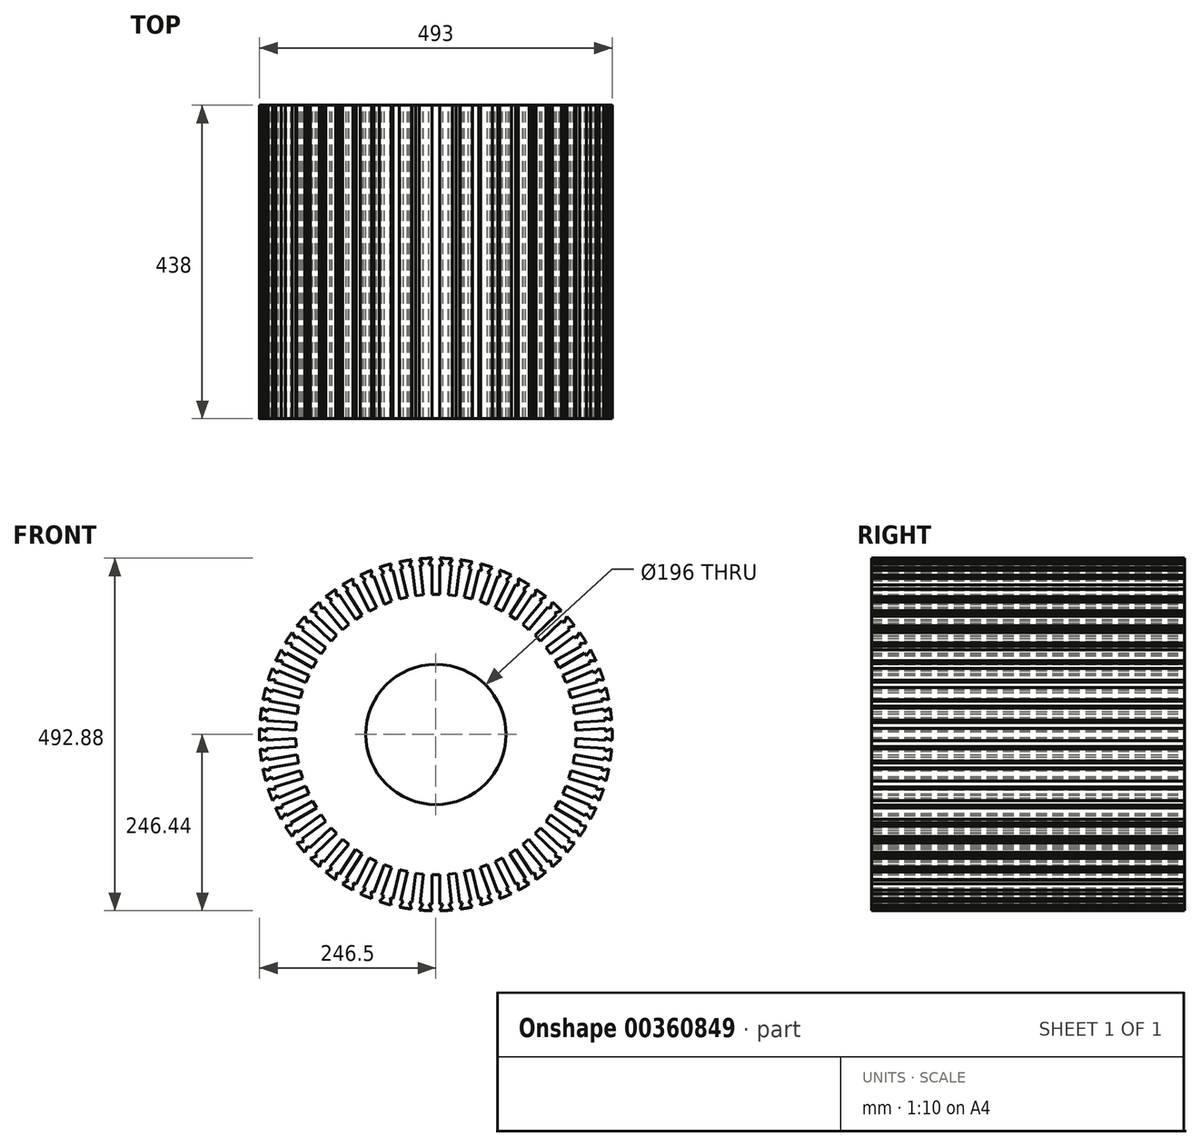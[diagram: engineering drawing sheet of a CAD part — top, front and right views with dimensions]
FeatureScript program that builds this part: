
annotation { "Feature Type Name" : "Feature", "Feature Type Description" : "" }
export const myFeature = defineFeature(function(context is Context, id is Id, definition is map)
    precondition{}
    {
        {
            var Q0;
            Q0=qCreatedBy(makeId("Front.planeOp"),FACE);
            var sketch = newSketch(context, id + "F0", { "sketchPlane" : qUnion([Q0])});
            skArc(sketch, "E0", {"start": v(-5.6, 246.44) * mm, "mid": v(-14.33, 246.08) * mm, "end": v(-23.05, 245.42) * mm});
            skLineSegment(sketch, "E1", {"start": v(0, -271.23) * mm, "end": v(0, 264.46) * mm, "construction": true});
            skLineSegment(sketch, "E2", {"start": v(0, 195.84) * mm, "end": v(-5.6, 195.84) * mm});
            skLineSegment(sketch, "E3", {"start": v(-5.6, 195.84) * mm, "end": v(-5.6, 237.27) * mm});
            skLineSegment(sketch, "E4.MirrorCS", {"start": v(5.6, 195.84) * mm, "end": v(5.6, 237.27) * mm});
            skLineSegment(sketch, "E5.MirrorCS", {"start": v(0, 195.84) * mm, "end": v(5.6, 195.84) * mm});
            skLineSegment(sketch, "E6", {"start": v(-5.6, 237.27) * mm, "end": v(-9.6, 237.27) * mm});
            skLineSegment(sketch, "E7", {"start": v(-9.6, 237.27) * mm, "end": v(-5.6, 246.44) * mm});
            skLineSegment(sketch, "E8.MirrorCS", {"start": v(9.6, 237.27) * mm, "end": v(5.6, 246.44) * mm});
            skLineSegment(sketch, "E9.MirrorCS", {"start": v(5.6, 237.27) * mm, "end": v(9.6, 237.27) * mm});
            skPoint(sketch, "E10.orphan", {"position": v(5.6, 246.44) * mm});
            skLineSegment(sketch, "E11.1.0", {"start": v(28.3, 193.86) * mm, "end": v(33.1, 235.02) * mm});
            skLineSegment(sketch, "E11.1.1", {"start": v(33.1, 235.02) * mm, "end": v(37.08, 234.55) * mm});
            skLineSegment(sketch, "E11.1.2", {"start": v(37.08, 234.55) * mm, "end": v(34.17, 244.12) * mm});
            skLineSegment(sketch, "E11.1.3", {"start": v(22.74, 194.51) * mm, "end": v(28.3, 193.86) * mm});
            skLineSegment(sketch, "E11.1.4", {"start": v(22.74, 194.51) * mm, "end": v(17.17, 195.16) * mm});
            skLineSegment(sketch, "E11.1.5", {"start": v(17.17, 195.16) * mm, "end": v(21.98, 236.32) * mm});
            skLineSegment(sketch, "E11.1.6", {"start": v(21.98, 236.32) * mm, "end": v(18.01, 236.78) * mm});
            skLineSegment(sketch, "E11.1.7", {"start": v(18.01, 236.78) * mm, "end": v(23.05, 245.42) * mm});
            skLineSegment(sketch, "E11.2.0", {"start": v(50.61, 189.27) * mm, "end": v(60.17, 229.58) * mm});
            skLineSegment(sketch, "E11.2.1", {"start": v(60.17, 229.58) * mm, "end": v(64.06, 228.66) * mm});
            skLineSegment(sketch, "E11.2.2", {"start": v(64.06, 228.66) * mm, "end": v(62.28, 238.5) * mm});
            skLineSegment(sketch, "E11.2.3", {"start": v(45.16, 190.56) * mm, "end": v(50.61, 189.27) * mm});
            skLineSegment(sketch, "E11.2.4", {"start": v(45.16, 190.56) * mm, "end": v(39.71, 191.85) * mm});
            skLineSegment(sketch, "E11.2.5", {"start": v(39.71, 191.85) * mm, "end": v(49.27, 232.17) * mm});
            skLineSegment(sketch, "E11.2.6", {"start": v(49.27, 232.17) * mm, "end": v(45.38, 233.09) * mm});
            skLineSegment(sketch, "E11.2.7", {"start": v(45.38, 233.09) * mm, "end": v(51.38, 241.09) * mm});
            skLineSegment(sketch, "E11.3.0", {"start": v(72.24, 182.11) * mm, "end": v(86.41, 221.05) * mm});
            skLineSegment(sketch, "E11.3.1", {"start": v(86.41, 221.05) * mm, "end": v(90.17, 219.68) * mm});
            skLineSegment(sketch, "E11.3.2", {"start": v(90.17, 219.68) * mm, "end": v(89.55, 229.66) * mm});
            skLineSegment(sketch, "E11.3.3", {"start": v(66.98, 184.03) * mm, "end": v(72.24, 182.11) * mm});
            skLineSegment(sketch, "E11.3.4", {"start": v(66.98, 184.03) * mm, "end": v(61.72, 185.94) * mm});
            skLineSegment(sketch, "E11.3.5", {"start": v(61.72, 185.94) * mm, "end": v(75.89, 224.88) * mm});
            skLineSegment(sketch, "E11.3.6", {"start": v(75.89, 224.88) * mm, "end": v(72.13, 226.25) * mm});
            skLineSegment(sketch, "E11.3.7", {"start": v(72.13, 226.25) * mm, "end": v(79.02, 233.49) * mm});
            skLineSegment(sketch, "E11.4.0", {"start": v(92.9, 172.5) * mm, "end": v(111.5, 209.52) * mm});
            skLineSegment(sketch, "E11.4.1", {"start": v(111.5, 209.52) * mm, "end": v(115.07, 207.72) * mm});
            skLineSegment(sketch, "E11.4.2", {"start": v(115.07, 207.72) * mm, "end": v(115.6, 217.71) * mm});
            skLineSegment(sketch, "E11.4.3", {"start": v(87.9, 175) * mm, "end": v(92.9, 172.5) * mm});
            skLineSegment(sketch, "E11.4.4", {"start": v(87.9, 175) * mm, "end": v(82.89, 177.52) * mm});
            skLineSegment(sketch, "E11.4.5", {"start": v(82.89, 177.52) * mm, "end": v(101.48, 214.55) * mm});
            skLineSegment(sketch, "E11.4.6", {"start": v(101.48, 214.55) * mm, "end": v(97.9, 216.34) * mm});
            skLineSegment(sketch, "E11.4.7", {"start": v(97.9, 216.34) * mm, "end": v(105.6, 222.74) * mm});
            skLineSegment(sketch, "E11.5.0", {"start": v(112.3, 160.54) * mm, "end": v(135.06, 195.16) * mm});
            skLineSegment(sketch, "E11.5.1", {"start": v(135.06, 195.16) * mm, "end": v(138.4, 192.96) * mm});
            skLineSegment(sketch, "E11.5.2", {"start": v(138.4, 192.96) * mm, "end": v(140.1, 202.82) * mm});
            skLineSegment(sketch, "E11.5.3", {"start": v(107.61, 163.62) * mm, "end": v(112.3, 160.54) * mm});
            skLineSegment(sketch, "E11.5.4", {"start": v(107.61, 163.62) * mm, "end": v(102.94, 166.7) * mm});
            skLineSegment(sketch, "E11.5.5", {"start": v(102.94, 166.7) * mm, "end": v(125.7, 201.31) * mm});
            skLineSegment(sketch, "E11.5.6", {"start": v(125.7, 201.31) * mm, "end": v(122.36, 203.51) * mm});
            skLineSegment(sketch, "E11.5.7", {"start": v(122.36, 203.51) * mm, "end": v(130.74, 208.97) * mm});
            skLineSegment(sketch, "E11.6.0", {"start": v(130.17, 146.42) * mm, "end": v(156.8, 178.16) * mm});
            skLineSegment(sketch, "E11.6.1", {"start": v(156.8, 178.16) * mm, "end": v(159.87, 175.59) * mm});
            skLineSegment(sketch, "E11.6.2", {"start": v(159.87, 175.59) * mm, "end": v(162.7, 185.18) * mm});
            skLineSegment(sketch, "E11.6.3", {"start": v(125.88, 150.02) * mm, "end": v(130.17, 146.42) * mm});
            skLineSegment(sketch, "E11.6.4", {"start": v(125.88, 150.02) * mm, "end": v(121.6, 153.62) * mm});
            skLineSegment(sketch, "E11.6.5", {"start": v(121.6, 153.62) * mm, "end": v(148.23, 185.36) * mm});
            skLineSegment(sketch, "E11.6.6", {"start": v(148.23, 185.36) * mm, "end": v(145.16, 187.93) * mm});
            skLineSegment(sketch, "E11.6.7", {"start": v(145.16, 187.93) * mm, "end": v(154.12, 192.38) * mm});
            skLineSegment(sketch, "E11.7.0", {"start": v(146.29, 130.32) * mm, "end": v(176.43, 158.75) * mm});
            skLineSegment(sketch, "E11.7.1", {"start": v(176.43, 158.75) * mm, "end": v(179.17, 155.84) * mm});
            skLineSegment(sketch, "E11.7.2", {"start": v(179.17, 155.84) * mm, "end": v(183.1, 165.04) * mm});
            skLineSegment(sketch, "E11.7.3", {"start": v(142.45, 134.4) * mm, "end": v(146.29, 130.32) * mm});
            skLineSegment(sketch, "E11.7.4", {"start": v(142.45, 134.4) * mm, "end": v(138.6, 138.46) * mm});
            skLineSegment(sketch, "E11.7.5", {"start": v(138.6, 138.46) * mm, "end": v(168.74, 166.9) * mm});
            skLineSegment(sketch, "E11.7.6", {"start": v(168.74, 166.9) * mm, "end": v(166, 169.8) * mm});
            skLineSegment(sketch, "E11.7.7", {"start": v(166, 169.8) * mm, "end": v(175.4, 173.19) * mm});
            skLineSegment(sketch, "E11.8.0", {"start": v(160.43, 112.45) * mm, "end": v(193.66, 137.2) * mm});
            skLineSegment(sketch, "E11.8.1", {"start": v(193.66, 137.2) * mm, "end": v(196.05, 133.99) * mm});
            skLineSegment(sketch, "E11.8.2", {"start": v(196.05, 133.99) * mm, "end": v(201.02, 142.67) * mm});
            skLineSegment(sketch, "E11.8.3", {"start": v(157.08, 116.95) * mm, "end": v(160.43, 112.45) * mm});
            skLineSegment(sketch, "E11.8.4", {"start": v(157.08, 116.95) * mm, "end": v(153.74, 121.44) * mm});
            skLineSegment(sketch, "E11.8.5", {"start": v(153.74, 121.44) * mm, "end": v(186.98, 146.18) * mm});
            skLineSegment(sketch, "E11.8.6", {"start": v(186.98, 146.18) * mm, "end": v(184.59, 149.39) * mm});
            skLineSegment(sketch, "E11.8.7", {"start": v(184.59, 149.39) * mm, "end": v(194.33, 151.65) * mm});
            skLineSegment(sketch, "E11.9.0", {"start": v(172.4, 93.07) * mm, "end": v(208.28, 113.79) * mm});
            skLineSegment(sketch, "E11.9.1", {"start": v(208.28, 113.79) * mm, "end": v(210.28, 110.32) * mm});
            skLineSegment(sketch, "E11.9.2", {"start": v(210.28, 110.32) * mm, "end": v(216.22, 118.37) * mm});
            skLineSegment(sketch, "E11.9.3", {"start": v(169.6, 97.92) * mm, "end": v(172.4, 93.07) * mm});
            skLineSegment(sketch, "E11.9.4", {"start": v(169.6, 97.92) * mm, "end": v(166.8, 102.77) * mm});
            skLineSegment(sketch, "E11.9.5", {"start": v(166.8, 102.77) * mm, "end": v(202.68, 123.49) * mm});
            skLineSegment(sketch, "E11.9.6", {"start": v(202.68, 123.49) * mm, "end": v(200.68, 126.95) * mm});
            skLineSegment(sketch, "E11.9.7", {"start": v(200.68, 126.95) * mm, "end": v(210.62, 128.07) * mm});
            skLineSegment(sketch, "E11.10.0", {"start": v(182.04, 72.42) * mm, "end": v(220.08, 88.84) * mm});
            skLineSegment(sketch, "E11.10.1", {"start": v(220.08, 88.84) * mm, "end": v(221.67, 85.16) * mm});
            skLineSegment(sketch, "E11.10.2", {"start": v(221.67, 85.16) * mm, "end": v(228.5, 92.47) * mm});
            skLineSegment(sketch, "E11.10.3", {"start": v(179.82, 77.57) * mm, "end": v(182.04, 72.42) * mm});
            skLineSegment(sketch, "E11.10.4", {"start": v(179.82, 77.57) * mm, "end": v(177.6, 82.7) * mm});
            skLineSegment(sketch, "E11.10.5", {"start": v(177.6, 82.7) * mm, "end": v(215.65, 99.12) * mm});
            skLineSegment(sketch, "E11.10.6", {"start": v(215.65, 99.12) * mm, "end": v(214.06, 102.8) * mm});
            skLineSegment(sketch, "E11.10.7", {"start": v(214.06, 102.8) * mm, "end": v(224.06, 102.75) * mm});
            skLineSegment(sketch, "E11.11.0", {"start": v(189.22, 50.8) * mm, "end": v(228.9, 62.69) * mm});
            skLineSegment(sketch, "E11.11.1", {"start": v(228.9, 62.69) * mm, "end": v(230.06, 58.85) * mm});
            skLineSegment(sketch, "E11.11.2", {"start": v(230.06, 58.85) * mm, "end": v(237.69, 65.31) * mm});
            skLineSegment(sketch, "E11.11.3", {"start": v(187.6, 56.17) * mm, "end": v(189.22, 50.8) * mm});
            skLineSegment(sketch, "E11.11.4", {"start": v(187.6, 56.17) * mm, "end": v(186, 61.53) * mm});
            skLineSegment(sketch, "E11.11.5", {"start": v(186, 61.53) * mm, "end": v(225.7, 73.41) * mm});
            skLineSegment(sketch, "E11.11.6", {"start": v(225.7, 73.41) * mm, "end": v(224.55, 77.25) * mm});
            skLineSegment(sketch, "E11.11.7", {"start": v(224.55, 77.25) * mm, "end": v(234.48, 76.04) * mm});
            skLineSegment(sketch, "E11.12.0", {"start": v(193.83, 28.5) * mm, "end": v(234.64, 35.69) * mm});
            skLineSegment(sketch, "E11.12.1", {"start": v(234.64, 35.69) * mm, "end": v(235.33, 31.75) * mm});
            skLineSegment(sketch, "E11.12.2", {"start": v(235.33, 31.75) * mm, "end": v(243.66, 37.28) * mm});
            skLineSegment(sketch, "E11.12.3", {"start": v(192.86, 34) * mm, "end": v(193.83, 28.5) * mm});
            skLineSegment(sketch, "E11.12.4", {"start": v(192.86, 34) * mm, "end": v(191.89, 39.52) * mm});
            skLineSegment(sketch, "E11.12.5", {"start": v(191.89, 39.52) * mm, "end": v(232.7, 46.72) * mm});
            skLineSegment(sketch, "E11.12.6", {"start": v(232.7, 46.72) * mm, "end": v(232, 50.66) * mm});
            skLineSegment(sketch, "E11.12.7", {"start": v(232, 50.66) * mm, "end": v(241.72, 48.3) * mm});
            skLineSegment(sketch, "E11.13.0", {"start": v(195.83, 5.8) * mm, "end": v(237.2, 8.2) * mm});
            skLineSegment(sketch, "E11.13.1", {"start": v(237.2, 8.2) * mm, "end": v(237.43, 4.21) * mm});
            skLineSegment(sketch, "E11.13.2", {"start": v(237.43, 4.21) * mm, "end": v(246.35, 8.74) * mm});
            skLineSegment(sketch, "E11.13.3", {"start": v(195.5, 11.39) * mm, "end": v(195.83, 5.8) * mm});
            skLineSegment(sketch, "E11.13.4", {"start": v(195.5, 11.39) * mm, "end": v(195.18, 16.98) * mm});
            skLineSegment(sketch, "E11.13.5", {"start": v(195.18, 16.98) * mm, "end": v(236.54, 19.39) * mm});
            skLineSegment(sketch, "E11.13.6", {"start": v(236.54, 19.39) * mm, "end": v(236.31, 23.38) * mm});
            skLineSegment(sketch, "E11.13.7", {"start": v(236.31, 23.38) * mm, "end": v(245.7, 19.92) * mm});
            skLineSegment(sketch, "E11.14.0", {"start": v(195.18, -16.98) * mm, "end": v(236.54, -19.39) * mm});
            skLineSegment(sketch, "E11.14.1", {"start": v(236.54, -19.39) * mm, "end": v(236.31, -23.38) * mm});
            skLineSegment(sketch, "E11.14.2", {"start": v(236.31, -23.38) * mm, "end": v(245.7, -19.92) * mm});
            skLineSegment(sketch, "E11.14.3", {"start": v(195.5, -11.39) * mm, "end": v(195.18, -16.98) * mm});
            skLineSegment(sketch, "E11.14.4", {"start": v(195.5, -11.39) * mm, "end": v(195.83, -5.8) * mm});
            skLineSegment(sketch, "E11.14.5", {"start": v(195.83, -5.8) * mm, "end": v(237.2, -8.2) * mm});
            skLineSegment(sketch, "E11.14.6", {"start": v(237.2, -8.2) * mm, "end": v(237.43, -4.21) * mm});
            skLineSegment(sketch, "E11.14.7", {"start": v(237.43, -4.21) * mm, "end": v(246.35, -8.74) * mm});
            skLineSegment(sketch, "E11.15.0", {"start": v(191.89, -39.52) * mm, "end": v(232.7, -46.72) * mm});
            skLineSegment(sketch, "E11.15.1", {"start": v(232.7, -46.72) * mm, "end": v(232, -50.66) * mm});
            skLineSegment(sketch, "E11.15.2", {"start": v(232, -50.66) * mm, "end": v(241.72, -48.3) * mm});
            skLineSegment(sketch, "E11.15.3", {"start": v(192.86, -34) * mm, "end": v(191.89, -39.52) * mm});
            skLineSegment(sketch, "E11.15.4", {"start": v(192.86, -34) * mm, "end": v(193.83, -28.5) * mm});
            skLineSegment(sketch, "E11.15.5", {"start": v(193.83, -28.5) * mm, "end": v(234.64, -35.69) * mm});
            skLineSegment(sketch, "E11.15.6", {"start": v(234.64, -35.69) * mm, "end": v(235.33, -31.75) * mm});
            skLineSegment(sketch, "E11.15.7", {"start": v(235.33, -31.75) * mm, "end": v(243.66, -37.28) * mm});
            skLineSegment(sketch, "E11.16.0", {"start": v(186, -61.53) * mm, "end": v(225.7, -73.41) * mm});
            skLineSegment(sketch, "E11.16.1", {"start": v(225.7, -73.41) * mm, "end": v(224.55, -77.25) * mm});
            skLineSegment(sketch, "E11.16.2", {"start": v(224.55, -77.25) * mm, "end": v(234.48, -76.04) * mm});
            skLineSegment(sketch, "E11.16.3", {"start": v(187.6, -56.17) * mm, "end": v(186, -61.53) * mm});
            skLineSegment(sketch, "E11.16.4", {"start": v(187.6, -56.17) * mm, "end": v(189.22, -50.8) * mm});
            skLineSegment(sketch, "E11.16.5", {"start": v(189.22, -50.8) * mm, "end": v(228.9, -62.69) * mm});
            skLineSegment(sketch, "E11.16.6", {"start": v(228.9, -62.69) * mm, "end": v(230.06, -58.85) * mm});
            skLineSegment(sketch, "E11.16.7", {"start": v(230.06, -58.85) * mm, "end": v(237.69, -65.31) * mm});
            skLineSegment(sketch, "E11.17.0", {"start": v(177.6, -82.7) * mm, "end": v(215.65, -99.12) * mm});
            skLineSegment(sketch, "E11.17.1", {"start": v(215.65, -99.12) * mm, "end": v(214.06, -102.8) * mm});
            skLineSegment(sketch, "E11.17.2", {"start": v(214.06, -102.8) * mm, "end": v(224.06, -102.75) * mm});
            skLineSegment(sketch, "E11.17.3", {"start": v(179.82, -77.57) * mm, "end": v(177.6, -82.7) * mm});
            skLineSegment(sketch, "E11.17.4", {"start": v(179.82, -77.57) * mm, "end": v(182.04, -72.42) * mm});
            skLineSegment(sketch, "E11.17.5", {"start": v(182.04, -72.42) * mm, "end": v(220.08, -88.84) * mm});
            skLineSegment(sketch, "E11.17.6", {"start": v(220.08, -88.84) * mm, "end": v(221.67, -85.16) * mm});
            skLineSegment(sketch, "E11.17.7", {"start": v(221.67, -85.16) * mm, "end": v(228.5, -92.47) * mm});
            skLineSegment(sketch, "E11.18.0", {"start": v(166.8, -102.77) * mm, "end": v(202.68, -123.49) * mm});
            skLineSegment(sketch, "E11.18.1", {"start": v(202.68, -123.49) * mm, "end": v(200.68, -126.95) * mm});
            skLineSegment(sketch, "E11.18.2", {"start": v(200.68, -126.95) * mm, "end": v(210.62, -128.07) * mm});
            skLineSegment(sketch, "E11.18.3", {"start": v(169.6, -97.92) * mm, "end": v(166.8, -102.77) * mm});
            skLineSegment(sketch, "E11.18.4", {"start": v(169.6, -97.92) * mm, "end": v(172.4, -93.07) * mm});
            skLineSegment(sketch, "E11.18.5", {"start": v(172.4, -93.07) * mm, "end": v(208.28, -113.79) * mm});
            skLineSegment(sketch, "E11.18.6", {"start": v(208.28, -113.79) * mm, "end": v(210.28, -110.32) * mm});
            skLineSegment(sketch, "E11.18.7", {"start": v(210.28, -110.32) * mm, "end": v(216.22, -118.37) * mm});
            skLineSegment(sketch, "E11.19.0", {"start": v(153.74, -121.44) * mm, "end": v(186.98, -146.18) * mm});
            skLineSegment(sketch, "E11.19.1", {"start": v(186.98, -146.18) * mm, "end": v(184.59, -149.39) * mm});
            skLineSegment(sketch, "E11.19.2", {"start": v(184.59, -149.39) * mm, "end": v(194.33, -151.65) * mm});
            skLineSegment(sketch, "E11.19.3", {"start": v(157.08, -116.95) * mm, "end": v(153.74, -121.44) * mm});
            skLineSegment(sketch, "E11.19.4", {"start": v(157.08, -116.95) * mm, "end": v(160.43, -112.45) * mm});
            skLineSegment(sketch, "E11.19.5", {"start": v(160.43, -112.45) * mm, "end": v(193.66, -137.2) * mm});
            skLineSegment(sketch, "E11.19.6", {"start": v(193.66, -137.2) * mm, "end": v(196.05, -133.99) * mm});
            skLineSegment(sketch, "E11.19.7", {"start": v(196.05, -133.99) * mm, "end": v(201.02, -142.67) * mm});
            skLineSegment(sketch, "E11.20.0", {"start": v(138.6, -138.46) * mm, "end": v(168.74, -166.9) * mm});
            skLineSegment(sketch, "E11.20.1", {"start": v(168.74, -166.9) * mm, "end": v(166, -169.8) * mm});
            skLineSegment(sketch, "E11.20.2", {"start": v(166, -169.8) * mm, "end": v(175.4, -173.19) * mm});
            skLineSegment(sketch, "E11.20.3", {"start": v(142.45, -134.4) * mm, "end": v(138.6, -138.46) * mm});
            skLineSegment(sketch, "E11.20.4", {"start": v(142.45, -134.4) * mm, "end": v(146.29, -130.32) * mm});
            skLineSegment(sketch, "E11.20.5", {"start": v(146.29, -130.32) * mm, "end": v(176.43, -158.75) * mm});
            skLineSegment(sketch, "E11.20.6", {"start": v(176.43, -158.75) * mm, "end": v(179.17, -155.84) * mm});
            skLineSegment(sketch, "E11.20.7", {"start": v(179.17, -155.84) * mm, "end": v(183.1, -165.04) * mm});
            skLineSegment(sketch, "E11.21.0", {"start": v(121.6, -153.62) * mm, "end": v(148.23, -185.36) * mm});
            skLineSegment(sketch, "E11.21.1", {"start": v(148.23, -185.36) * mm, "end": v(145.16, -187.93) * mm});
            skLineSegment(sketch, "E11.21.2", {"start": v(145.16, -187.93) * mm, "end": v(154.12, -192.38) * mm});
            skLineSegment(sketch, "E11.21.3", {"start": v(125.88, -150.02) * mm, "end": v(121.6, -153.62) * mm});
            skLineSegment(sketch, "E11.21.4", {"start": v(125.88, -150.02) * mm, "end": v(130.17, -146.42) * mm});
            skLineSegment(sketch, "E11.21.5", {"start": v(130.17, -146.42) * mm, "end": v(156.8, -178.16) * mm});
            skLineSegment(sketch, "E11.21.6", {"start": v(156.8, -178.16) * mm, "end": v(159.87, -175.59) * mm});
            skLineSegment(sketch, "E11.21.7", {"start": v(159.87, -175.59) * mm, "end": v(162.7, -185.18) * mm});
            skLineSegment(sketch, "E11.22.0", {"start": v(102.94, -166.7) * mm, "end": v(125.7, -201.31) * mm});
            skLineSegment(sketch, "E11.22.1", {"start": v(125.7, -201.31) * mm, "end": v(122.36, -203.51) * mm});
            skLineSegment(sketch, "E11.22.2", {"start": v(122.36, -203.51) * mm, "end": v(130.74, -208.97) * mm});
            skLineSegment(sketch, "E11.22.3", {"start": v(107.61, -163.62) * mm, "end": v(102.94, -166.7) * mm});
            skLineSegment(sketch, "E11.22.4", {"start": v(107.61, -163.62) * mm, "end": v(112.3, -160.54) * mm});
            skLineSegment(sketch, "E11.22.5", {"start": v(112.3, -160.54) * mm, "end": v(135.06, -195.16) * mm});
            skLineSegment(sketch, "E11.22.6", {"start": v(135.06, -195.16) * mm, "end": v(138.4, -192.96) * mm});
            skLineSegment(sketch, "E11.22.7", {"start": v(138.4, -192.96) * mm, "end": v(140.1, -202.82) * mm});
            skLineSegment(sketch, "E11.23.0", {"start": v(82.89, -177.52) * mm, "end": v(101.48, -214.55) * mm});
            skLineSegment(sketch, "E11.23.1", {"start": v(101.48, -214.55) * mm, "end": v(97.9, -216.34) * mm});
            skLineSegment(sketch, "E11.23.2", {"start": v(97.9, -216.34) * mm, "end": v(105.6, -222.74) * mm});
            skLineSegment(sketch, "E11.23.3", {"start": v(87.9, -175) * mm, "end": v(82.89, -177.52) * mm});
            skLineSegment(sketch, "E11.23.4", {"start": v(87.9, -175) * mm, "end": v(92.9, -172.5) * mm});
            skLineSegment(sketch, "E11.23.5", {"start": v(92.9, -172.5) * mm, "end": v(111.5, -209.52) * mm});
            skLineSegment(sketch, "E11.23.6", {"start": v(111.5, -209.52) * mm, "end": v(115.07, -207.72) * mm});
            skLineSegment(sketch, "E11.23.7", {"start": v(115.07, -207.72) * mm, "end": v(115.6, -217.71) * mm});
            skLineSegment(sketch, "E11.24.0", {"start": v(61.72, -185.94) * mm, "end": v(75.89, -224.88) * mm});
            skLineSegment(sketch, "E11.24.1", {"start": v(75.89, -224.88) * mm, "end": v(72.13, -226.25) * mm});
            skLineSegment(sketch, "E11.24.2", {"start": v(72.13, -226.25) * mm, "end": v(79.02, -233.49) * mm});
            skLineSegment(sketch, "E11.24.3", {"start": v(66.98, -184.03) * mm, "end": v(61.72, -185.94) * mm});
            skLineSegment(sketch, "E11.24.4", {"start": v(66.98, -184.03) * mm, "end": v(72.24, -182.11) * mm});
            skLineSegment(sketch, "E11.24.5", {"start": v(72.24, -182.11) * mm, "end": v(86.41, -221.05) * mm});
            skLineSegment(sketch, "E11.24.6", {"start": v(86.41, -221.05) * mm, "end": v(90.17, -219.68) * mm});
            skLineSegment(sketch, "E11.24.7", {"start": v(90.17, -219.68) * mm, "end": v(89.55, -229.66) * mm});
            skLineSegment(sketch, "E11.25.0", {"start": v(39.71, -191.85) * mm, "end": v(49.27, -232.17) * mm});
            skLineSegment(sketch, "E11.25.1", {"start": v(49.27, -232.17) * mm, "end": v(45.38, -233.09) * mm});
            skLineSegment(sketch, "E11.25.2", {"start": v(45.38, -233.09) * mm, "end": v(51.38, -241.09) * mm});
            skLineSegment(sketch, "E11.25.3", {"start": v(45.16, -190.56) * mm, "end": v(39.71, -191.85) * mm});
            skLineSegment(sketch, "E11.25.4", {"start": v(45.16, -190.56) * mm, "end": v(50.61, -189.27) * mm});
            skLineSegment(sketch, "E11.25.5", {"start": v(50.61, -189.27) * mm, "end": v(60.17, -229.58) * mm});
            skLineSegment(sketch, "E11.25.6", {"start": v(60.17, -229.58) * mm, "end": v(64.06, -228.66) * mm});
            skLineSegment(sketch, "E11.25.7", {"start": v(64.06, -228.66) * mm, "end": v(62.28, -238.5) * mm});
            skLineSegment(sketch, "E11.26.0", {"start": v(17.17, -195.16) * mm, "end": v(21.98, -236.32) * mm});
            skLineSegment(sketch, "E11.26.1", {"start": v(21.98, -236.32) * mm, "end": v(18.01, -236.78) * mm});
            skLineSegment(sketch, "E11.26.2", {"start": v(18.01, -236.78) * mm, "end": v(23.05, -245.42) * mm});
            skLineSegment(sketch, "E11.26.3", {"start": v(22.74, -194.51) * mm, "end": v(17.17, -195.16) * mm});
            skLineSegment(sketch, "E11.26.4", {"start": v(22.74, -194.51) * mm, "end": v(28.3, -193.86) * mm});
            skLineSegment(sketch, "E11.26.5", {"start": v(28.3, -193.86) * mm, "end": v(33.1, -235.02) * mm});
            skLineSegment(sketch, "E11.26.6", {"start": v(33.1, -235.02) * mm, "end": v(37.08, -234.55) * mm});
            skLineSegment(sketch, "E11.26.7", {"start": v(37.08, -234.55) * mm, "end": v(34.17, -244.12) * mm});
            skLineSegment(sketch, "E11.27.0", {"start": v(-5.6, -195.84) * mm, "end": v(-5.6, -237.27) * mm});
            skLineSegment(sketch, "E11.27.1", {"start": v(-5.6, -237.27) * mm, "end": v(-9.6, -237.27) * mm});
            skLineSegment(sketch, "E11.27.2", {"start": v(-9.6, -237.27) * mm, "end": v(-5.6, -246.44) * mm});
            skLineSegment(sketch, "E11.27.3", {"start": v(0, -195.84) * mm, "end": v(-5.6, -195.84) * mm});
            skLineSegment(sketch, "E11.27.4", {"start": v(0, -195.84) * mm, "end": v(5.6, -195.84) * mm});
            skLineSegment(sketch, "E11.27.5", {"start": v(5.6, -195.84) * mm, "end": v(5.6, -237.27) * mm});
            skLineSegment(sketch, "E11.27.6", {"start": v(5.6, -237.27) * mm, "end": v(9.6, -237.27) * mm});
            skLineSegment(sketch, "E11.27.7", {"start": v(9.6, -237.27) * mm, "end": v(5.6, -246.44) * mm});
            skLineSegment(sketch, "E11.28.0", {"start": v(-28.3, -193.86) * mm, "end": v(-33.1, -235.02) * mm});
            skLineSegment(sketch, "E11.28.1", {"start": v(-33.1, -235.02) * mm, "end": v(-37.08, -234.55) * mm});
            skLineSegment(sketch, "E11.28.2", {"start": v(-37.08, -234.55) * mm, "end": v(-34.17, -244.12) * mm});
            skLineSegment(sketch, "E11.28.3", {"start": v(-22.74, -194.51) * mm, "end": v(-28.3, -193.86) * mm});
            skLineSegment(sketch, "E11.28.4", {"start": v(-22.74, -194.51) * mm, "end": v(-17.17, -195.16) * mm});
            skLineSegment(sketch, "E11.28.5", {"start": v(-17.17, -195.16) * mm, "end": v(-21.98, -236.32) * mm});
            skLineSegment(sketch, "E11.28.6", {"start": v(-21.98, -236.32) * mm, "end": v(-18.01, -236.78) * mm});
            skLineSegment(sketch, "E11.28.7", {"start": v(-18.01, -236.78) * mm, "end": v(-23.05, -245.42) * mm});
            skLineSegment(sketch, "E11.29.0", {"start": v(-50.61, -189.27) * mm, "end": v(-60.17, -229.58) * mm});
            skLineSegment(sketch, "E11.29.1", {"start": v(-60.17, -229.58) * mm, "end": v(-64.06, -228.66) * mm});
            skLineSegment(sketch, "E11.29.2", {"start": v(-64.06, -228.66) * mm, "end": v(-62.28, -238.5) * mm});
            skLineSegment(sketch, "E11.29.3", {"start": v(-45.16, -190.56) * mm, "end": v(-50.61, -189.27) * mm});
            skLineSegment(sketch, "E11.29.4", {"start": v(-45.16, -190.56) * mm, "end": v(-39.71, -191.85) * mm});
            skLineSegment(sketch, "E11.29.5", {"start": v(-39.71, -191.85) * mm, "end": v(-49.27, -232.17) * mm});
            skLineSegment(sketch, "E11.29.6", {"start": v(-49.27, -232.17) * mm, "end": v(-45.38, -233.09) * mm});
            skLineSegment(sketch, "E11.29.7", {"start": v(-45.38, -233.09) * mm, "end": v(-51.38, -241.09) * mm});
            skLineSegment(sketch, "E11.30.0", {"start": v(-72.24, -182.11) * mm, "end": v(-86.41, -221.05) * mm});
            skLineSegment(sketch, "E11.30.1", {"start": v(-86.41, -221.05) * mm, "end": v(-90.17, -219.68) * mm});
            skLineSegment(sketch, "E11.30.2", {"start": v(-90.17, -219.68) * mm, "end": v(-89.55, -229.66) * mm});
            skLineSegment(sketch, "E11.30.3", {"start": v(-66.98, -184.03) * mm, "end": v(-72.24, -182.11) * mm});
            skLineSegment(sketch, "E11.30.4", {"start": v(-66.98, -184.03) * mm, "end": v(-61.72, -185.94) * mm});
            skLineSegment(sketch, "E11.30.5", {"start": v(-61.72, -185.94) * mm, "end": v(-75.89, -224.88) * mm});
            skLineSegment(sketch, "E11.30.6", {"start": v(-75.89, -224.88) * mm, "end": v(-72.13, -226.25) * mm});
            skLineSegment(sketch, "E11.30.7", {"start": v(-72.13, -226.25) * mm, "end": v(-79.02, -233.49) * mm});
            skLineSegment(sketch, "E11.31.0", {"start": v(-92.9, -172.5) * mm, "end": v(-111.5, -209.52) * mm});
            skLineSegment(sketch, "E11.31.1", {"start": v(-111.5, -209.52) * mm, "end": v(-115.07, -207.72) * mm});
            skLineSegment(sketch, "E11.31.2", {"start": v(-115.07, -207.72) * mm, "end": v(-115.6, -217.71) * mm});
            skLineSegment(sketch, "E11.31.3", {"start": v(-87.9, -175) * mm, "end": v(-92.9, -172.5) * mm});
            skLineSegment(sketch, "E11.31.4", {"start": v(-87.9, -175) * mm, "end": v(-82.89, -177.52) * mm});
            skLineSegment(sketch, "E11.31.5", {"start": v(-82.89, -177.52) * mm, "end": v(-101.48, -214.55) * mm});
            skLineSegment(sketch, "E11.31.6", {"start": v(-101.48, -214.55) * mm, "end": v(-97.9, -216.34) * mm});
            skLineSegment(sketch, "E11.31.7", {"start": v(-97.9, -216.34) * mm, "end": v(-105.6, -222.74) * mm});
            skLineSegment(sketch, "E11.32.0", {"start": v(-112.3, -160.54) * mm, "end": v(-135.06, -195.16) * mm});
            skLineSegment(sketch, "E11.32.1", {"start": v(-135.06, -195.16) * mm, "end": v(-138.4, -192.96) * mm});
            skLineSegment(sketch, "E11.32.2", {"start": v(-138.4, -192.96) * mm, "end": v(-140.1, -202.82) * mm});
            skLineSegment(sketch, "E11.32.3", {"start": v(-107.61, -163.62) * mm, "end": v(-112.3, -160.54) * mm});
            skLineSegment(sketch, "E11.32.4", {"start": v(-107.61, -163.62) * mm, "end": v(-102.94, -166.7) * mm});
            skLineSegment(sketch, "E11.32.5", {"start": v(-102.94, -166.7) * mm, "end": v(-125.7, -201.31) * mm});
            skLineSegment(sketch, "E11.32.6", {"start": v(-125.7, -201.31) * mm, "end": v(-122.36, -203.51) * mm});
            skLineSegment(sketch, "E11.32.7", {"start": v(-122.36, -203.51) * mm, "end": v(-130.74, -208.97) * mm});
            skLineSegment(sketch, "E11.33.0", {"start": v(-130.17, -146.42) * mm, "end": v(-156.8, -178.16) * mm});
            skLineSegment(sketch, "E11.33.1", {"start": v(-156.8, -178.16) * mm, "end": v(-159.87, -175.59) * mm});
            skLineSegment(sketch, "E11.33.2", {"start": v(-159.87, -175.59) * mm, "end": v(-162.7, -185.18) * mm});
            skLineSegment(sketch, "E11.33.3", {"start": v(-125.88, -150.02) * mm, "end": v(-130.17, -146.42) * mm});
            skLineSegment(sketch, "E11.33.4", {"start": v(-125.88, -150.02) * mm, "end": v(-121.6, -153.62) * mm});
            skLineSegment(sketch, "E11.33.5", {"start": v(-121.6, -153.62) * mm, "end": v(-148.23, -185.36) * mm});
            skLineSegment(sketch, "E11.33.6", {"start": v(-148.23, -185.36) * mm, "end": v(-145.16, -187.93) * mm});
            skLineSegment(sketch, "E11.33.7", {"start": v(-145.16, -187.93) * mm, "end": v(-154.12, -192.38) * mm});
            skLineSegment(sketch, "E11.34.0", {"start": v(-146.29, -130.32) * mm, "end": v(-176.43, -158.75) * mm});
            skLineSegment(sketch, "E11.34.1", {"start": v(-176.43, -158.75) * mm, "end": v(-179.17, -155.84) * mm});
            skLineSegment(sketch, "E11.34.2", {"start": v(-179.17, -155.84) * mm, "end": v(-183.1, -165.04) * mm});
            skLineSegment(sketch, "E11.34.3", {"start": v(-142.45, -134.4) * mm, "end": v(-146.29, -130.32) * mm});
            skLineSegment(sketch, "E11.34.4", {"start": v(-142.45, -134.4) * mm, "end": v(-138.6, -138.46) * mm});
            skLineSegment(sketch, "E11.34.5", {"start": v(-138.6, -138.46) * mm, "end": v(-168.74, -166.9) * mm});
            skLineSegment(sketch, "E11.34.6", {"start": v(-168.74, -166.9) * mm, "end": v(-166, -169.8) * mm});
            skLineSegment(sketch, "E11.34.7", {"start": v(-166, -169.8) * mm, "end": v(-175.4, -173.19) * mm});
            skLineSegment(sketch, "E11.35.0", {"start": v(-160.43, -112.45) * mm, "end": v(-193.66, -137.2) * mm});
            skLineSegment(sketch, "E11.35.1", {"start": v(-193.66, -137.2) * mm, "end": v(-196.05, -133.99) * mm});
            skLineSegment(sketch, "E11.35.2", {"start": v(-196.05, -133.99) * mm, "end": v(-201.02, -142.67) * mm});
            skLineSegment(sketch, "E11.35.3", {"start": v(-157.08, -116.95) * mm, "end": v(-160.43, -112.45) * mm});
            skLineSegment(sketch, "E11.35.4", {"start": v(-157.08, -116.95) * mm, "end": v(-153.74, -121.44) * mm});
            skLineSegment(sketch, "E11.35.5", {"start": v(-153.74, -121.44) * mm, "end": v(-186.98, -146.18) * mm});
            skLineSegment(sketch, "E11.35.6", {"start": v(-186.98, -146.18) * mm, "end": v(-184.59, -149.39) * mm});
            skLineSegment(sketch, "E11.35.7", {"start": v(-184.59, -149.39) * mm, "end": v(-194.33, -151.65) * mm});
            skLineSegment(sketch, "E11.36.0", {"start": v(-172.4, -93.07) * mm, "end": v(-208.28, -113.79) * mm});
            skLineSegment(sketch, "E11.36.1", {"start": v(-208.28, -113.79) * mm, "end": v(-210.28, -110.32) * mm});
            skLineSegment(sketch, "E11.36.2", {"start": v(-210.28, -110.32) * mm, "end": v(-216.22, -118.37) * mm});
            skLineSegment(sketch, "E11.36.3", {"start": v(-169.6, -97.92) * mm, "end": v(-172.4, -93.07) * mm});
            skLineSegment(sketch, "E11.36.4", {"start": v(-169.6, -97.92) * mm, "end": v(-166.8, -102.77) * mm});
            skLineSegment(sketch, "E11.36.5", {"start": v(-166.8, -102.77) * mm, "end": v(-202.68, -123.49) * mm});
            skLineSegment(sketch, "E11.36.6", {"start": v(-202.68, -123.49) * mm, "end": v(-200.68, -126.95) * mm});
            skLineSegment(sketch, "E11.36.7", {"start": v(-200.68, -126.95) * mm, "end": v(-210.62, -128.07) * mm});
            skLineSegment(sketch, "E11.37.0", {"start": v(-182.04, -72.42) * mm, "end": v(-220.08, -88.84) * mm});
            skLineSegment(sketch, "E11.37.1", {"start": v(-220.08, -88.84) * mm, "end": v(-221.67, -85.16) * mm});
            skLineSegment(sketch, "E11.37.2", {"start": v(-221.67, -85.16) * mm, "end": v(-228.5, -92.47) * mm});
            skLineSegment(sketch, "E11.37.3", {"start": v(-179.82, -77.57) * mm, "end": v(-182.04, -72.42) * mm});
            skLineSegment(sketch, "E11.37.4", {"start": v(-179.82, -77.57) * mm, "end": v(-177.6, -82.7) * mm});
            skLineSegment(sketch, "E11.37.5", {"start": v(-177.6, -82.7) * mm, "end": v(-215.65, -99.12) * mm});
            skLineSegment(sketch, "E11.37.6", {"start": v(-215.65, -99.12) * mm, "end": v(-214.06, -102.8) * mm});
            skLineSegment(sketch, "E11.37.7", {"start": v(-214.06, -102.8) * mm, "end": v(-224.06, -102.75) * mm});
            skLineSegment(sketch, "E11.38.0", {"start": v(-189.22, -50.8) * mm, "end": v(-228.9, -62.69) * mm});
            skLineSegment(sketch, "E11.38.1", {"start": v(-228.9, -62.69) * mm, "end": v(-230.06, -58.85) * mm});
            skLineSegment(sketch, "E11.38.2", {"start": v(-230.06, -58.85) * mm, "end": v(-237.69, -65.31) * mm});
            skLineSegment(sketch, "E11.38.3", {"start": v(-187.6, -56.17) * mm, "end": v(-189.22, -50.8) * mm});
            skLineSegment(sketch, "E11.38.4", {"start": v(-187.6, -56.17) * mm, "end": v(-186, -61.53) * mm});
            skLineSegment(sketch, "E11.38.5", {"start": v(-186, -61.53) * mm, "end": v(-225.7, -73.41) * mm});
            skLineSegment(sketch, "E11.38.6", {"start": v(-225.7, -73.41) * mm, "end": v(-224.55, -77.25) * mm});
            skLineSegment(sketch, "E11.38.7", {"start": v(-224.55, -77.25) * mm, "end": v(-234.48, -76.04) * mm});
            skLineSegment(sketch, "E11.39.0", {"start": v(-193.83, -28.5) * mm, "end": v(-234.64, -35.69) * mm});
            skLineSegment(sketch, "E11.39.1", {"start": v(-234.64, -35.69) * mm, "end": v(-235.33, -31.75) * mm});
            skLineSegment(sketch, "E11.39.2", {"start": v(-235.33, -31.75) * mm, "end": v(-243.66, -37.28) * mm});
            skLineSegment(sketch, "E11.39.3", {"start": v(-192.86, -34) * mm, "end": v(-193.83, -28.5) * mm});
            skLineSegment(sketch, "E11.39.4", {"start": v(-192.86, -34) * mm, "end": v(-191.89, -39.52) * mm});
            skLineSegment(sketch, "E11.39.5", {"start": v(-191.89, -39.52) * mm, "end": v(-232.7, -46.72) * mm});
            skLineSegment(sketch, "E11.39.6", {"start": v(-232.7, -46.72) * mm, "end": v(-232, -50.66) * mm});
            skLineSegment(sketch, "E11.39.7", {"start": v(-232, -50.66) * mm, "end": v(-241.72, -48.3) * mm});
            skLineSegment(sketch, "E11.40.0", {"start": v(-195.83, -5.8) * mm, "end": v(-237.2, -8.2) * mm});
            skLineSegment(sketch, "E11.40.1", {"start": v(-237.2, -8.2) * mm, "end": v(-237.43, -4.21) * mm});
            skLineSegment(sketch, "E11.40.2", {"start": v(-237.43, -4.21) * mm, "end": v(-246.35, -8.74) * mm});
            skLineSegment(sketch, "E11.40.3", {"start": v(-195.5, -11.39) * mm, "end": v(-195.83, -5.8) * mm});
            skLineSegment(sketch, "E11.40.4", {"start": v(-195.5, -11.39) * mm, "end": v(-195.18, -16.98) * mm});
            skLineSegment(sketch, "E11.40.5", {"start": v(-195.18, -16.98) * mm, "end": v(-236.54, -19.39) * mm});
            skLineSegment(sketch, "E11.40.6", {"start": v(-236.54, -19.39) * mm, "end": v(-236.31, -23.38) * mm});
            skLineSegment(sketch, "E11.40.7", {"start": v(-236.31, -23.38) * mm, "end": v(-245.7, -19.92) * mm});
            skLineSegment(sketch, "E11.41.0", {"start": v(-195.18, 16.98) * mm, "end": v(-236.54, 19.39) * mm});
            skLineSegment(sketch, "E11.41.1", {"start": v(-236.54, 19.39) * mm, "end": v(-236.31, 23.38) * mm});
            skLineSegment(sketch, "E11.41.2", {"start": v(-236.31, 23.38) * mm, "end": v(-245.7, 19.92) * mm});
            skLineSegment(sketch, "E11.41.3", {"start": v(-195.5, 11.39) * mm, "end": v(-195.18, 16.98) * mm});
            skLineSegment(sketch, "E11.41.4", {"start": v(-195.5, 11.39) * mm, "end": v(-195.83, 5.8) * mm});
            skLineSegment(sketch, "E11.41.5", {"start": v(-195.83, 5.8) * mm, "end": v(-237.2, 8.2) * mm});
            skLineSegment(sketch, "E11.41.6", {"start": v(-237.2, 8.2) * mm, "end": v(-237.43, 4.21) * mm});
            skLineSegment(sketch, "E11.41.7", {"start": v(-237.43, 4.21) * mm, "end": v(-246.35, 8.74) * mm});
            skLineSegment(sketch, "E11.42.0", {"start": v(-191.89, 39.52) * mm, "end": v(-232.7, 46.72) * mm});
            skLineSegment(sketch, "E11.42.1", {"start": v(-232.7, 46.72) * mm, "end": v(-232, 50.66) * mm});
            skLineSegment(sketch, "E11.42.2", {"start": v(-232, 50.66) * mm, "end": v(-241.72, 48.3) * mm});
            skLineSegment(sketch, "E11.42.3", {"start": v(-192.86, 34) * mm, "end": v(-191.89, 39.52) * mm});
            skLineSegment(sketch, "E11.42.4", {"start": v(-192.86, 34) * mm, "end": v(-193.83, 28.5) * mm});
            skLineSegment(sketch, "E11.42.5", {"start": v(-193.83, 28.5) * mm, "end": v(-234.64, 35.69) * mm});
            skLineSegment(sketch, "E11.42.6", {"start": v(-234.64, 35.69) * mm, "end": v(-235.33, 31.75) * mm});
            skLineSegment(sketch, "E11.42.7", {"start": v(-235.33, 31.75) * mm, "end": v(-243.66, 37.28) * mm});
            skLineSegment(sketch, "E11.43.0", {"start": v(-186, 61.53) * mm, "end": v(-225.7, 73.41) * mm});
            skLineSegment(sketch, "E11.43.1", {"start": v(-225.7, 73.41) * mm, "end": v(-224.55, 77.25) * mm});
            skLineSegment(sketch, "E11.43.2", {"start": v(-224.55, 77.25) * mm, "end": v(-234.48, 76.04) * mm});
            skLineSegment(sketch, "E11.43.3", {"start": v(-187.6, 56.17) * mm, "end": v(-186, 61.53) * mm});
            skLineSegment(sketch, "E11.43.4", {"start": v(-187.6, 56.17) * mm, "end": v(-189.22, 50.8) * mm});
            skLineSegment(sketch, "E11.43.5", {"start": v(-189.22, 50.8) * mm, "end": v(-228.9, 62.69) * mm});
            skLineSegment(sketch, "E11.43.6", {"start": v(-228.9, 62.69) * mm, "end": v(-230.06, 58.85) * mm});
            skLineSegment(sketch, "E11.43.7", {"start": v(-230.06, 58.85) * mm, "end": v(-237.69, 65.31) * mm});
            skLineSegment(sketch, "E11.44.0", {"start": v(-177.6, 82.7) * mm, "end": v(-215.65, 99.12) * mm});
            skLineSegment(sketch, "E11.44.1", {"start": v(-215.65, 99.12) * mm, "end": v(-214.06, 102.8) * mm});
            skLineSegment(sketch, "E11.44.2", {"start": v(-214.06, 102.8) * mm, "end": v(-224.06, 102.75) * mm});
            skLineSegment(sketch, "E11.44.3", {"start": v(-179.82, 77.57) * mm, "end": v(-177.6, 82.7) * mm});
            skLineSegment(sketch, "E11.44.4", {"start": v(-179.82, 77.57) * mm, "end": v(-182.04, 72.42) * mm});
            skLineSegment(sketch, "E11.44.5", {"start": v(-182.04, 72.42) * mm, "end": v(-220.08, 88.84) * mm});
            skLineSegment(sketch, "E11.44.6", {"start": v(-220.08, 88.84) * mm, "end": v(-221.67, 85.16) * mm});
            skLineSegment(sketch, "E11.44.7", {"start": v(-221.67, 85.16) * mm, "end": v(-228.5, 92.47) * mm});
            skLineSegment(sketch, "E11.45.0", {"start": v(-166.8, 102.77) * mm, "end": v(-202.68, 123.49) * mm});
            skLineSegment(sketch, "E11.45.1", {"start": v(-202.68, 123.49) * mm, "end": v(-200.68, 126.95) * mm});
            skLineSegment(sketch, "E11.45.2", {"start": v(-200.68, 126.95) * mm, "end": v(-210.62, 128.07) * mm});
            skLineSegment(sketch, "E11.45.3", {"start": v(-169.6, 97.92) * mm, "end": v(-166.8, 102.77) * mm});
            skLineSegment(sketch, "E11.45.4", {"start": v(-169.6, 97.92) * mm, "end": v(-172.4, 93.07) * mm});
            skLineSegment(sketch, "E11.45.5", {"start": v(-172.4, 93.07) * mm, "end": v(-208.28, 113.79) * mm});
            skLineSegment(sketch, "E11.45.6", {"start": v(-208.28, 113.79) * mm, "end": v(-210.28, 110.32) * mm});
            skLineSegment(sketch, "E11.45.7", {"start": v(-210.28, 110.32) * mm, "end": v(-216.22, 118.37) * mm});
            skLineSegment(sketch, "E11.46.0", {"start": v(-153.74, 121.44) * mm, "end": v(-186.98, 146.18) * mm});
            skLineSegment(sketch, "E11.46.1", {"start": v(-186.98, 146.18) * mm, "end": v(-184.59, 149.39) * mm});
            skLineSegment(sketch, "E11.46.2", {"start": v(-184.59, 149.39) * mm, "end": v(-194.33, 151.65) * mm});
            skLineSegment(sketch, "E11.46.3", {"start": v(-157.08, 116.95) * mm, "end": v(-153.74, 121.44) * mm});
            skLineSegment(sketch, "E11.46.4", {"start": v(-157.08, 116.95) * mm, "end": v(-160.43, 112.45) * mm});
            skLineSegment(sketch, "E11.46.5", {"start": v(-160.43, 112.45) * mm, "end": v(-193.66, 137.2) * mm});
            skLineSegment(sketch, "E11.46.6", {"start": v(-193.66, 137.2) * mm, "end": v(-196.05, 133.99) * mm});
            skLineSegment(sketch, "E11.46.7", {"start": v(-196.05, 133.99) * mm, "end": v(-201.02, 142.67) * mm});
            skLineSegment(sketch, "E11.47.0", {"start": v(-138.6, 138.46) * mm, "end": v(-168.74, 166.9) * mm});
            skLineSegment(sketch, "E11.47.1", {"start": v(-168.74, 166.9) * mm, "end": v(-166, 169.8) * mm});
            skLineSegment(sketch, "E11.47.2", {"start": v(-166, 169.8) * mm, "end": v(-175.4, 173.19) * mm});
            skLineSegment(sketch, "E11.47.3", {"start": v(-142.45, 134.4) * mm, "end": v(-138.6, 138.46) * mm});
            skLineSegment(sketch, "E11.47.4", {"start": v(-142.45, 134.4) * mm, "end": v(-146.29, 130.32) * mm});
            skLineSegment(sketch, "E11.47.5", {"start": v(-146.29, 130.32) * mm, "end": v(-176.43, 158.75) * mm});
            skLineSegment(sketch, "E11.47.6", {"start": v(-176.43, 158.75) * mm, "end": v(-179.17, 155.84) * mm});
            skLineSegment(sketch, "E11.47.7", {"start": v(-179.17, 155.84) * mm, "end": v(-183.1, 165.04) * mm});
            skLineSegment(sketch, "E11.48.0", {"start": v(-121.6, 153.62) * mm, "end": v(-148.23, 185.36) * mm});
            skLineSegment(sketch, "E11.48.1", {"start": v(-148.23, 185.36) * mm, "end": v(-145.16, 187.93) * mm});
            skLineSegment(sketch, "E11.48.2", {"start": v(-145.16, 187.93) * mm, "end": v(-154.12, 192.38) * mm});
            skLineSegment(sketch, "E11.48.3", {"start": v(-125.88, 150.02) * mm, "end": v(-121.6, 153.62) * mm});
            skLineSegment(sketch, "E11.48.4", {"start": v(-125.88, 150.02) * mm, "end": v(-130.17, 146.42) * mm});
            skLineSegment(sketch, "E11.48.5", {"start": v(-130.17, 146.42) * mm, "end": v(-156.8, 178.16) * mm});
            skLineSegment(sketch, "E11.48.6", {"start": v(-156.8, 178.16) * mm, "end": v(-159.87, 175.59) * mm});
            skLineSegment(sketch, "E11.48.7", {"start": v(-159.87, 175.59) * mm, "end": v(-162.7, 185.18) * mm});
            skLineSegment(sketch, "E11.49.0", {"start": v(-102.94, 166.7) * mm, "end": v(-125.7, 201.31) * mm});
            skLineSegment(sketch, "E11.49.1", {"start": v(-125.7, 201.31) * mm, "end": v(-122.36, 203.51) * mm});
            skLineSegment(sketch, "E11.49.2", {"start": v(-122.36, 203.51) * mm, "end": v(-130.74, 208.97) * mm});
            skLineSegment(sketch, "E11.49.3", {"start": v(-107.61, 163.62) * mm, "end": v(-102.94, 166.7) * mm});
            skLineSegment(sketch, "E11.49.4", {"start": v(-107.61, 163.62) * mm, "end": v(-112.3, 160.54) * mm});
            skLineSegment(sketch, "E11.49.5", {"start": v(-112.3, 160.54) * mm, "end": v(-135.06, 195.16) * mm});
            skLineSegment(sketch, "E11.49.6", {"start": v(-135.06, 195.16) * mm, "end": v(-138.4, 192.96) * mm});
            skLineSegment(sketch, "E11.49.7", {"start": v(-138.4, 192.96) * mm, "end": v(-140.1, 202.82) * mm});
            skLineSegment(sketch, "E11.50.0", {"start": v(-82.89, 177.52) * mm, "end": v(-101.48, 214.55) * mm});
            skLineSegment(sketch, "E11.50.1", {"start": v(-101.48, 214.55) * mm, "end": v(-97.9, 216.34) * mm});
            skLineSegment(sketch, "E11.50.2", {"start": v(-97.9, 216.34) * mm, "end": v(-105.6, 222.74) * mm});
            skLineSegment(sketch, "E11.50.3", {"start": v(-87.9, 175) * mm, "end": v(-82.89, 177.52) * mm});
            skLineSegment(sketch, "E11.50.4", {"start": v(-87.9, 175) * mm, "end": v(-92.9, 172.5) * mm});
            skLineSegment(sketch, "E11.50.5", {"start": v(-92.9, 172.5) * mm, "end": v(-111.5, 209.52) * mm});
            skLineSegment(sketch, "E11.50.6", {"start": v(-111.5, 209.52) * mm, "end": v(-115.07, 207.72) * mm});
            skLineSegment(sketch, "E11.50.7", {"start": v(-115.07, 207.72) * mm, "end": v(-115.6, 217.71) * mm});
            skLineSegment(sketch, "E11.51.0", {"start": v(-61.72, 185.94) * mm, "end": v(-75.89, 224.88) * mm});
            skLineSegment(sketch, "E11.51.1", {"start": v(-75.89, 224.88) * mm, "end": v(-72.13, 226.25) * mm});
            skLineSegment(sketch, "E11.51.2", {"start": v(-72.13, 226.25) * mm, "end": v(-79.02, 233.49) * mm});
            skLineSegment(sketch, "E11.51.3", {"start": v(-66.98, 184.03) * mm, "end": v(-61.72, 185.94) * mm});
            skLineSegment(sketch, "E11.51.4", {"start": v(-66.98, 184.03) * mm, "end": v(-72.24, 182.11) * mm});
            skLineSegment(sketch, "E11.51.5", {"start": v(-72.24, 182.11) * mm, "end": v(-86.41, 221.05) * mm});
            skLineSegment(sketch, "E11.51.6", {"start": v(-86.41, 221.05) * mm, "end": v(-90.17, 219.68) * mm});
            skLineSegment(sketch, "E11.51.7", {"start": v(-90.17, 219.68) * mm, "end": v(-89.55, 229.66) * mm});
            skLineSegment(sketch, "E11.52.0", {"start": v(-39.71, 191.85) * mm, "end": v(-49.27, 232.17) * mm});
            skLineSegment(sketch, "E11.52.1", {"start": v(-49.27, 232.17) * mm, "end": v(-45.38, 233.09) * mm});
            skLineSegment(sketch, "E11.52.2", {"start": v(-45.38, 233.09) * mm, "end": v(-51.38, 241.09) * mm});
            skLineSegment(sketch, "E11.52.3", {"start": v(-45.16, 190.56) * mm, "end": v(-39.71, 191.85) * mm});
            skLineSegment(sketch, "E11.52.4", {"start": v(-45.16, 190.56) * mm, "end": v(-50.61, 189.27) * mm});
            skLineSegment(sketch, "E11.52.5", {"start": v(-50.61, 189.27) * mm, "end": v(-60.17, 229.58) * mm});
            skLineSegment(sketch, "E11.52.6", {"start": v(-60.17, 229.58) * mm, "end": v(-64.06, 228.66) * mm});
            skLineSegment(sketch, "E11.52.7", {"start": v(-64.06, 228.66) * mm, "end": v(-62.28, 238.5) * mm});
            skLineSegment(sketch, "E11.53.0", {"start": v(-17.17, 195.16) * mm, "end": v(-21.98, 236.32) * mm});
            skLineSegment(sketch, "E11.53.1", {"start": v(-21.98, 236.32) * mm, "end": v(-18.01, 236.78) * mm});
            skLineSegment(sketch, "E11.53.2", {"start": v(-18.01, 236.78) * mm, "end": v(-23.05, 245.42) * mm});
            skLineSegment(sketch, "E11.53.3", {"start": v(-22.74, 194.51) * mm, "end": v(-17.17, 195.16) * mm});
            skLineSegment(sketch, "E11.53.4", {"start": v(-22.74, 194.51) * mm, "end": v(-28.3, 193.86) * mm});
            skLineSegment(sketch, "E11.53.5", {"start": v(-28.3, 193.86) * mm, "end": v(-33.1, 235.02) * mm});
            skLineSegment(sketch, "E11.53.6", {"start": v(-33.1, 235.02) * mm, "end": v(-37.08, 234.55) * mm});
            skLineSegment(sketch, "E11.53.7", {"start": v(-37.08, 234.55) * mm, "end": v(-34.17, 244.12) * mm});
            skLineSegment(sketch, "E11.anchor1", {"start": v(0, 0) * mm, "end": v(5.6, 195.84) * mm, "construction": true});
            skLineSegment(sketch, "E11.anchor2", {"start": v(0, 0) * mm, "end": v(-17.17, 195.16) * mm, "construction": true});
            skArc(sketch, "E12.trimOffspring", {"start": v(-34.17, 244.12) * mm, "mid": v(-42.8, 242.76) * mm, "end": v(-51.38, 241.09) * mm});
            skArc(sketch, "E13.trimOffspring", {"start": v(-62.28, 238.5) * mm, "mid": v(-70.7, 236.14) * mm, "end": v(-79.02, 233.49) * mm});
            skArc(sketch, "E14.trimOffspring", {"start": v(-89.55, 229.66) * mm, "mid": v(-97.63, 226.34) * mm, "end": v(-105.6, 222.74) * mm});
            skArc(sketch, "E15.trimOffspring", {"start": v(-115.6, 217.71) * mm, "mid": v(-123.25, 213.48) * mm, "end": v(-130.74, 208.97) * mm});
            skArc(sketch, "E16.trimOffspring", {"start": v(-140.1, 202.82) * mm, "mid": v(-147.2, 197.72) * mm, "end": v(-154.12, 192.38) * mm});
            skArc(sketch, "E17.trimOffspring", {"start": v(-162.7, 185.18) * mm, "mid": v(-169.16, 179.3) * mm, "end": v(-175.4, 173.19) * mm});
            skArc(sketch, "E18.trimOffspring", {"start": v(-183.1, 165.04) * mm, "mid": v(-188.83, 158.45) * mm, "end": v(-194.33, 151.65) * mm});
            skArc(sketch, "E19.trimOffspring", {"start": v(-201.02, 142.67) * mm, "mid": v(-205.95, 135.45) * mm, "end": v(-210.62, 128.07) * mm});
            skArc(sketch, "E20.trimOffspring", {"start": v(-216.22, 118.37) * mm, "mid": v(-220.28, 110.63) * mm, "end": v(-224.06, 102.75) * mm});
            skArc(sketch, "E21.trimOffspring", {"start": v(-228.5, 92.47) * mm, "mid": v(-231.63, 84.3) * mm, "end": v(-234.48, 76.04) * mm});
            skArc(sketch, "E22.trimOffspring", {"start": v(-237.69, 65.31) * mm, "mid": v(-239.86, 56.85) * mm, "end": v(-241.72, 48.3) * mm});
            skArc(sketch, "E23.trimOffspring", {"start": v(-243.66, 37.28) * mm, "mid": v(-244.83, 28.62) * mm, "end": v(-245.7, 19.92) * mm});
            skArc(sketch, "E24.trimOffspring", {"start": v(-246.35, 8.74) * mm, "mid": v(-246.5, 0) * mm, "end": v(-246.35, -8.74) * mm});
            skArc(sketch, "E25.trimOffspring", {"start": v(-245.7, -19.92) * mm, "mid": v(-244.83, -28.62) * mm, "end": v(-243.66, -37.28) * mm});
            skArc(sketch, "E26.trimOffspring", {"start": v(-241.72, -48.3) * mm, "mid": v(-239.86, -56.85) * mm, "end": v(-237.69, -65.31) * mm});
            skArc(sketch, "E27.trimOffspring", {"start": v(-234.48, -76.04) * mm, "mid": v(-231.63, -84.3) * mm, "end": v(-228.5, -92.47) * mm});
            skArc(sketch, "E28.trimOffspring", {"start": v(-224.06, -102.75) * mm, "mid": v(-220.28, -110.63) * mm, "end": v(-216.22, -118.37) * mm});
            skArc(sketch, "E29.trimOffspring", {"start": v(-210.62, -128.07) * mm, "mid": v(-205.95, -135.45) * mm, "end": v(-201.02, -142.67) * mm});
            skArc(sketch, "E30.trimOffspring", {"start": v(-194.33, -151.65) * mm, "mid": v(-188.83, -158.45) * mm, "end": v(-183.1, -165.04) * mm});
            skArc(sketch, "E31.trimOffspring", {"start": v(-175.4, -173.19) * mm, "mid": v(-169.16, -179.3) * mm, "end": v(-162.7, -185.18) * mm});
            skArc(sketch, "E32.trimOffspring", {"start": v(-154.12, -192.38) * mm, "mid": v(-147.2, -197.72) * mm, "end": v(-140.1, -202.82) * mm});
            skArc(sketch, "E33.trimOffspring", {"start": v(-130.74, -208.97) * mm, "mid": v(-123.25, -213.48) * mm, "end": v(-115.6, -217.71) * mm});
            skArc(sketch, "E34.trimOffspring", {"start": v(-105.6, -222.74) * mm, "mid": v(-97.63, -226.34) * mm, "end": v(-89.55, -229.66) * mm});
            skArc(sketch, "E35.trimOffspring", {"start": v(-79.02, -233.49) * mm, "mid": v(-70.7, -236.14) * mm, "end": v(-62.28, -238.5) * mm});
            skArc(sketch, "E36.trimOffspring", {"start": v(-51.38, -241.09) * mm, "mid": v(-42.8, -242.76) * mm, "end": v(-34.17, -244.12) * mm});
            skArc(sketch, "E37.trimOffspring", {"start": v(-23.05, -245.42) * mm, "mid": v(-14.33, -246.08) * mm, "end": v(-5.6, -246.44) * mm});
            skArc(sketch, "E38.trimOffspring", {"start": v(5.6, -246.44) * mm, "mid": v(14.33, -246.08) * mm, "end": v(23.05, -245.42) * mm});
            skArc(sketch, "E39.trimOffspring", {"start": v(34.17, -244.12) * mm, "mid": v(42.8, -242.76) * mm, "end": v(51.38, -241.09) * mm});
            skArc(sketch, "E40.trimOffspring", {"start": v(62.28, -238.5) * mm, "mid": v(70.7, -236.14) * mm, "end": v(79.02, -233.49) * mm});
            skArc(sketch, "E41.trimOffspring", {"start": v(89.55, -229.66) * mm, "mid": v(97.63, -226.34) * mm, "end": v(105.6, -222.74) * mm});
            skArc(sketch, "E42.trimOffspring", {"start": v(115.6, -217.71) * mm, "mid": v(123.25, -213.48) * mm, "end": v(130.74, -208.97) * mm});
            skArc(sketch, "E43.trimOffspring", {"start": v(140.1, -202.82) * mm, "mid": v(147.2, -197.72) * mm, "end": v(154.12, -192.38) * mm});
            skArc(sketch, "E44.trimOffspring", {"start": v(162.7, -185.18) * mm, "mid": v(169.16, -179.3) * mm, "end": v(175.4, -173.19) * mm});
            skArc(sketch, "E45.trimOffspring", {"start": v(183.1, -165.04) * mm, "mid": v(188.83, -158.45) * mm, "end": v(194.33, -151.65) * mm});
            skArc(sketch, "E46.trimOffspring", {"start": v(201.02, -142.67) * mm, "mid": v(205.95, -135.45) * mm, "end": v(210.62, -128.07) * mm});
            skArc(sketch, "E47.trimOffspring", {"start": v(216.22, -118.37) * mm, "mid": v(220.28, -110.63) * mm, "end": v(224.06, -102.75) * mm});
            skArc(sketch, "E48.trimOffspring", {"start": v(228.5, -92.47) * mm, "mid": v(231.63, -84.3) * mm, "end": v(234.48, -76.04) * mm});
            skArc(sketch, "E49.trimOffspring", {"start": v(237.69, -65.31) * mm, "mid": v(239.86, -56.85) * mm, "end": v(241.72, -48.3) * mm});
            skArc(sketch, "E50.trimOffspring", {"start": v(243.66, -37.28) * mm, "mid": v(244.83, -28.62) * mm, "end": v(245.7, -19.92) * mm});
            skArc(sketch, "E51.trimOffspring", {"start": v(246.35, -8.74) * mm, "mid": v(246.5, 0) * mm, "end": v(246.35, 8.74) * mm});
            skArc(sketch, "E52.trimOffspring", {"start": v(245.7, 19.92) * mm, "mid": v(244.83, 28.62) * mm, "end": v(243.66, 37.28) * mm});
            skArc(sketch, "E53.trimOffspring", {"start": v(241.72, 48.3) * mm, "mid": v(239.86, 56.85) * mm, "end": v(237.69, 65.31) * mm});
            skArc(sketch, "E54.trimOffspring", {"start": v(234.48, 76.04) * mm, "mid": v(231.63, 84.3) * mm, "end": v(228.5, 92.47) * mm});
            skArc(sketch, "E55.trimOffspring", {"start": v(224.06, 102.75) * mm, "mid": v(220.28, 110.63) * mm, "end": v(216.22, 118.37) * mm});
            skArc(sketch, "E56.trimOffspring", {"start": v(210.62, 128.07) * mm, "mid": v(205.95, 135.45) * mm, "end": v(201.02, 142.67) * mm});
            skArc(sketch, "E57.trimOffspring", {"start": v(194.33, 151.65) * mm, "mid": v(188.83, 158.45) * mm, "end": v(183.1, 165.04) * mm});
            skArc(sketch, "E58.trimOffspring", {"start": v(175.4, 173.19) * mm, "mid": v(169.16, 179.3) * mm, "end": v(162.7, 185.18) * mm});
            skArc(sketch, "E59.trimOffspring", {"start": v(154.12, 192.38) * mm, "mid": v(147.2, 197.72) * mm, "end": v(140.1, 202.82) * mm});
            skArc(sketch, "E60.trimOffspring", {"start": v(130.74, 208.97) * mm, "mid": v(123.25, 213.48) * mm, "end": v(115.6, 217.71) * mm});
            skArc(sketch, "E61.trimOffspring", {"start": v(105.6, 222.74) * mm, "mid": v(97.63, 226.34) * mm, "end": v(89.55, 229.66) * mm});
            skArc(sketch, "E62.trimOffspring", {"start": v(79.02, 233.49) * mm, "mid": v(70.7, 236.14) * mm, "end": v(62.28, 238.5) * mm});
            skArc(sketch, "E63.trimOffspring", {"start": v(51.38, 241.09) * mm, "mid": v(42.8, 242.76) * mm, "end": v(34.17, 244.12) * mm});
            skArc(sketch, "E64.trimOffspring", {"start": v(23.05, 245.42) * mm, "mid": v(14.33, 246.08) * mm, "end": v(5.6, 246.44) * mm});
            skCircle(sketch, "E65", {"center": v(0, 0) * mm, "radius": 98 * mm});
            skSolve(sketch);
        }
        {
            var Q0;
            Q0=qSketchRegion(id+"F0",true);
            extrude(context, id + "F1", {"entities" : qUnion([Q0]), "depth" : 438 * mm});
        }
    });
